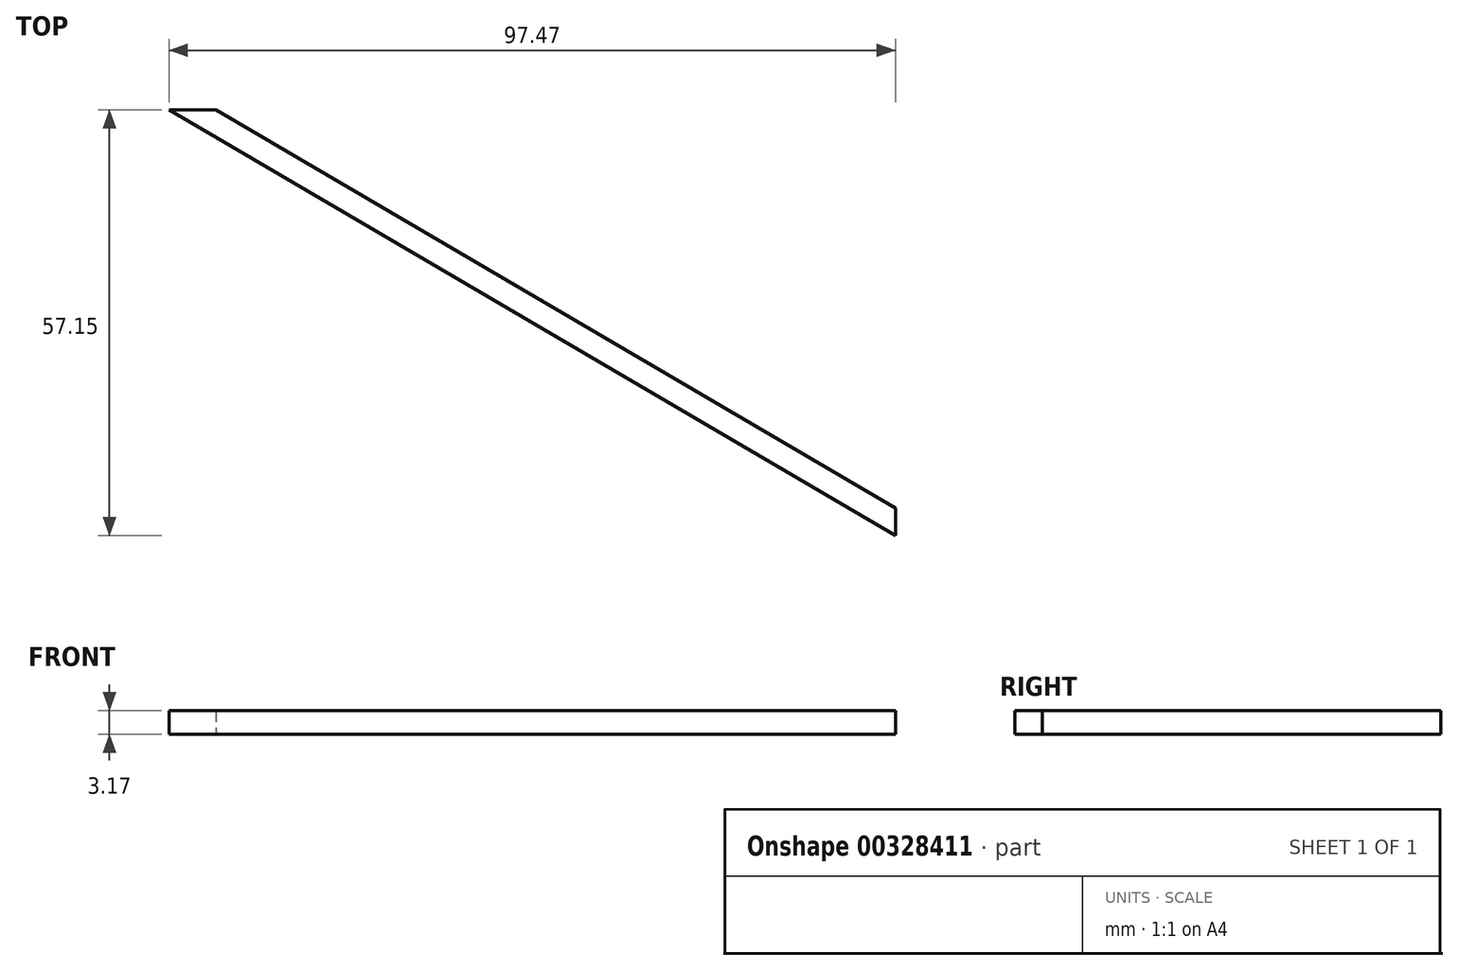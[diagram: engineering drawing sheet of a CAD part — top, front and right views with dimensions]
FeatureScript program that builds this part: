
annotation { "Feature Type Name" : "Feature", "Feature Type Description" : "" }
export const myFeature = defineFeature(function(context is Context, id is Id, definition is map)
    precondition{}
    {
        {
            var Q0;
            Q0=qCreatedBy(makeId("Top.planeOp"),FACE);
            var sketch = newSketch(context, id + "F0", { "sketchPlane" : qUnion([Q0])});
            skLineSegment(sketch, "E0", {"start": v(0, 0) * mm, "end": v(97.47, 0) * mm});
            skLineSegment(sketch, "E1", {"start": v(0, 0) * mm, "end": v(0, 57.15) * mm});
            skLineSegment(sketch, "E2", {"start": v(0, 57.15) * mm, "end": v(97.47, 0) * mm});
            skLineSegment(sketch, "E3", {"start": v(0, 57.15) * mm, "end": v(97.47, 57.15) * mm});
            skLineSegment(sketch, "E4", {"start": v(97.47, 57.15) * mm, "end": v(97.47, 0) * mm});
            skLineSegment(sketch, "E5", {"start": v(6.28, 57.15) * mm, "end": v(97.47, 3.68) * mm});
            skLineSegment(sketch, "E6", {"start": v(0, 0) * mm, "end": v(98.83, 0) * mm});
            skSolve(sketch);
        }
        {
            var Q0;
            {var subQ0=sQuery(id+"F0.wireOp",EDGE,"E2");Q0=makeQuery(id+"F0.imprint","IMPRINT",FACE,{"disambiguationData":[TD([[makeQuery(id+"F0.imprint","IMPRINT",EDGE,{"derivedFrom":subQ0}),1.0]])]});}
            extrude(context, id + "F1", {"entities" : qUnion([Q0]), "depth" : 3.17 * mm});
        }
    });
